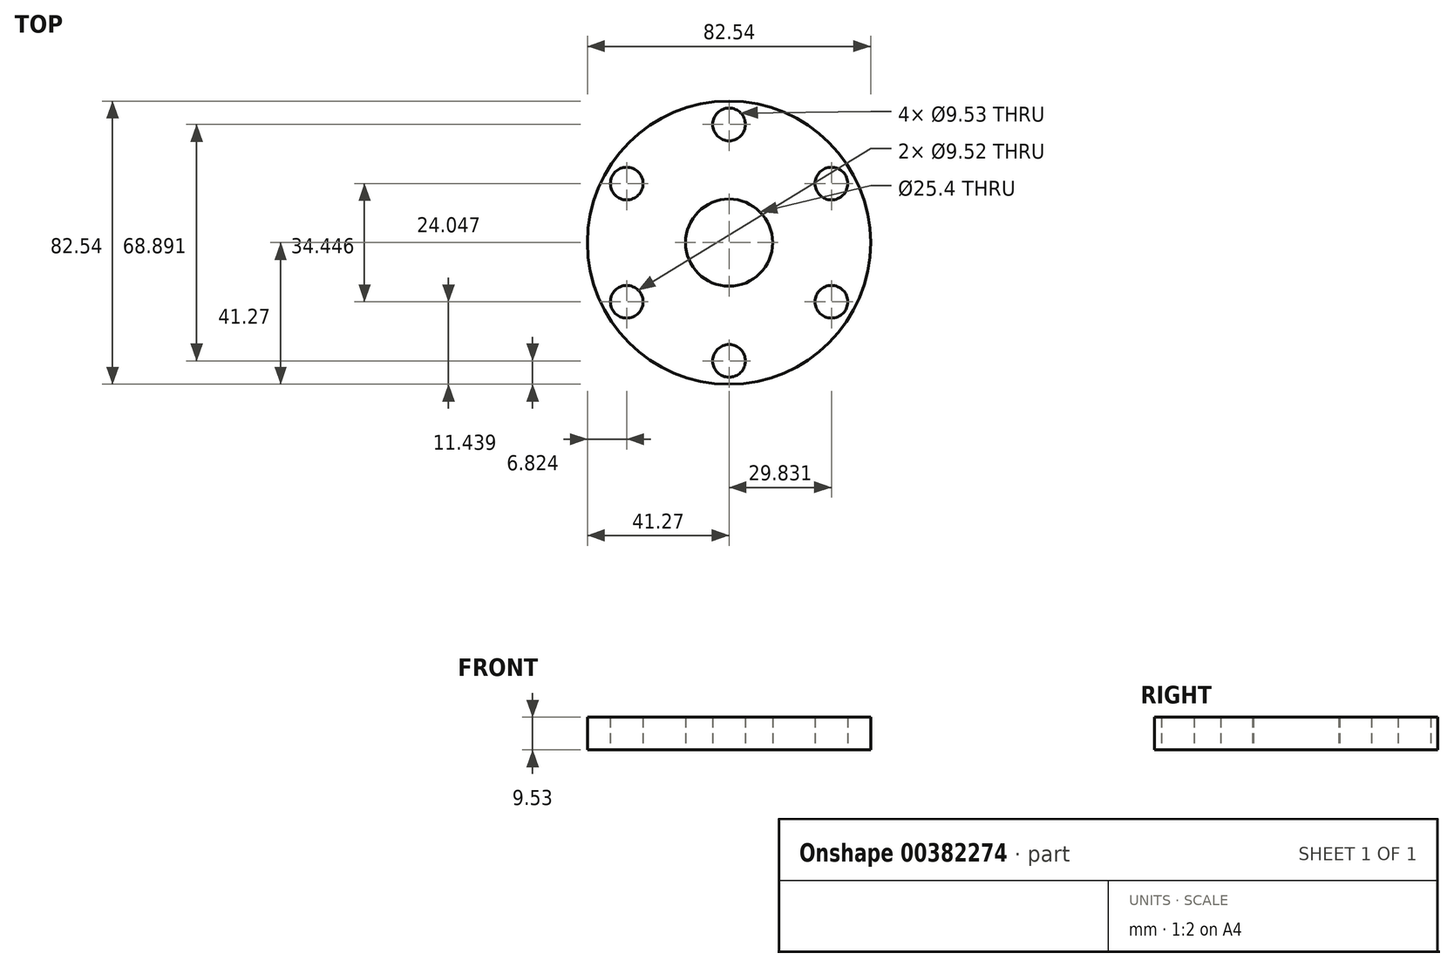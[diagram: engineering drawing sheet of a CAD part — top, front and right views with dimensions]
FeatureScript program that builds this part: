
annotation { "Feature Type Name" : "Feature", "Feature Type Description" : "" }
export const myFeature = defineFeature(function(context is Context, id is Id, definition is map)
    precondition{}
    {
        {
            var Q0;
            Q0=qCreatedBy(makeId("Top.planeOp"),FACE);
            var sketch = newSketch(context, id + "F0", { "sketchPlane" : qUnion([Q0])});
            skCircle(sketch, "E0", {"center": v(0, 0) * mm, "radius": 41.27 * mm});
            skCircle(sketch, "E1.cCircle", {"center": v(0, 0) * mm, "radius": 29.83 * mm, "construction": true});
            skLineSegment(sketch, "E1.0", {"start": v(29.83, 17.22) * mm, "end": v(29.83, -17.22) * mm});
            skLineSegment(sketch, "E1.1", {"start": v(29.83, -17.22) * mm, "end": v(0, -34.45) * mm});
            skLineSegment(sketch, "E1.2", {"start": v(0, -34.45) * mm, "end": v(-29.83, -17.22) * mm});
            skLineSegment(sketch, "E1.3", {"start": v(-29.83, -17.22) * mm, "end": v(-29.83, 17.22) * mm});
            skLineSegment(sketch, "E1.4", {"start": v(-29.83, 17.22) * mm, "end": v(0, 34.45) * mm});
            skLineSegment(sketch, "E1.5", {"start": v(0, 34.45) * mm, "end": v(29.83, 17.22) * mm});
            skPoint(sketch, "E1.0.midPoint", {"position": v(29.83, 0) * mm});
            skCircle(sketch, "E2", {"center": v(0, 34.45) * mm, "radius": 4.77 * mm});
            skCircle(sketch, "E3", {"center": v(29.83, 17.22) * mm, "radius": 4.76 * mm});
            skCircle(sketch, "E4", {"center": v(29.83, -17.22) * mm, "radius": 4.77 * mm});
            skCircle(sketch, "E5", {"center": v(0, -34.45) * mm, "radius": 4.77 * mm});
            skCircle(sketch, "E6", {"center": v(-29.83, 17.22) * mm, "radius": 4.76 * mm});
            skCircle(sketch, "E7", {"center": v(-29.83, -17.22) * mm, "radius": 4.76 * mm});
            skCircle(sketch, "E8", {"center": v(0, 0) * mm, "radius": 12.7 * mm});
            skSolve(sketch);
        }
        {
            var Q0;
            Q0 = qSketchRegion(id + "F0", true);
            var Q1;
            Q1=makeQuery(id+"F0.imprint","IMPRINT",FACE,{"disambiguationData":[TD([[makeQuery(id+"F0.imprint","IMPRINT",EDGE,{"derivedFrom":sQuery(id+"F0.wireOp",EDGE,"LcDseN9k-ZboN-G9mR-OHll-LmikN7JHm8x6")}),-1.0]])]});
            var Q2;
            Q2=makeQuery(id+"F0.imprint","IMPRINT",FACE,{"disambiguationData":[TD([[makeQuery(id+"F0.imprint","IMPRINT",EDGE,{"derivedFrom":sQuery(id+"F0.wireOp",EDGE,"E8")}),-1.0]])]});
            extrude(context, id + "F1", {"entities" : qUnion([Q0, Q1, Q2]), "depth" : 9.52 * mm});
        }
    });
